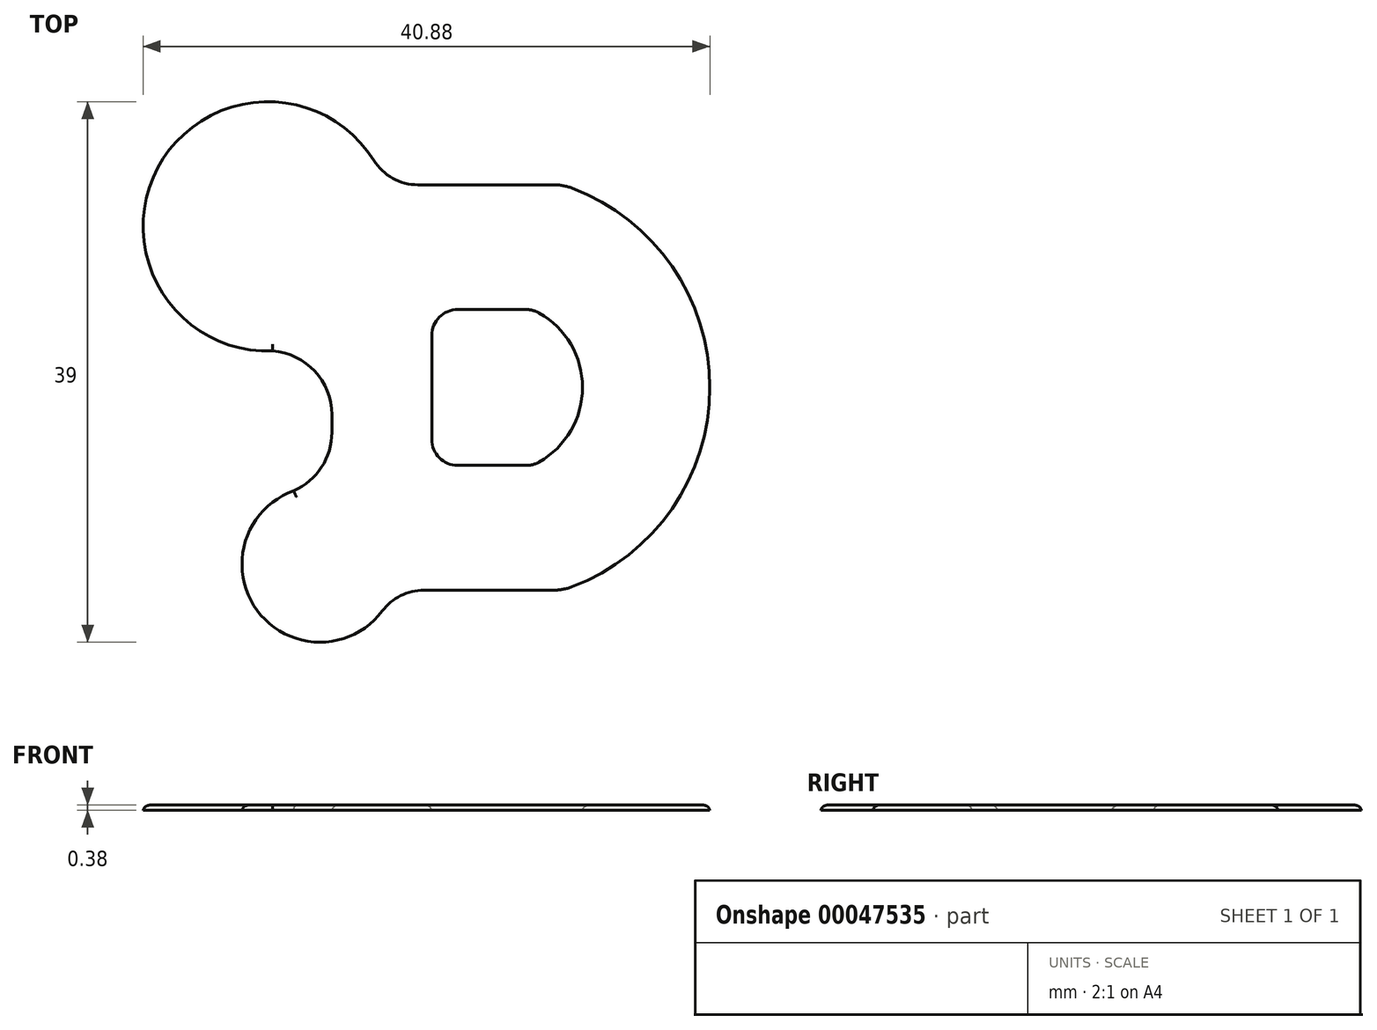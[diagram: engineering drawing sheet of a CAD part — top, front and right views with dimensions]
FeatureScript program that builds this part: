
annotation { "Feature Type Name" : "Feature", "Feature Type Description" : "" }
export const myFeature = defineFeature(function(context is Context, id is Id, definition is map)
    precondition{}
    {
        {
            var Q0;
            Q0=qCreatedBy(makeId("Top.planeOp"),FACE);
            var sketch = newSketch(context, id + "F0", { "sketchPlane" : qUnion([Q0])});
            skArc(sketch, "E0", {"start": v(20.36, 12.7) * mm, "mid": v(-21.2, 11.25) * mm, "end": v(0.9, -23.98) * mm});
            skArc(sketch, "E1", {"start": v(5.1, -50.82) * mm, "mid": v(-2.12, -73.84) * mm, "end": v(22, -74) * mm});
            skArc(sketch, "E2.trimOffspring", {"start": v(52.15, -45.35) * mm, "mid": v(60.5, -31) * mm, "end": v(52.15, -16.65) * mm});
            skArc(sketch, "E3.trimOffspring", {"start": v(58.49, -69.35) * mm, "mid": v(85, -31) * mm, "end": v(58.49, 7.35) * mm});
            skLineSegment(sketch, "E4", {"start": v(31.5, -21) * mm, "end": v(31.5, -41) * mm});
            skLineSegment(sketch, "E5", {"start": v(49.68, -16) * mm, "end": v(36.5, -16) * mm});
            skLineSegment(sketch, "E6", {"start": v(49.68, -46) * mm, "end": v(36.5, -46) * mm});
            skPoint(sketch, "E7.visualSharp", {"position": v(31.5, -16) * mm});
            skArc(sketch, "E7.filletArc", {"start": v(36.5, -16) * mm, "mid": v(32.96, -17.46) * mm, "end": v(31.5, -21) * mm});
            skPoint(sketch, "E8.visualSharp", {"position": v(31.5, -46) * mm});
            skArc(sketch, "E8.filletArc", {"start": v(31.5, -41) * mm, "mid": v(32.96, -44.54) * mm, "end": v(36.5, -46) * mm});
            skPoint(sketch, "E9.visualSharp", {"position": v(50.87, -16) * mm});
            skArc(sketch, "E9.filletArc", {"start": v(52.15, -16.65) * mm, "mid": v(50.96, -16.17) * mm, "end": v(49.68, -16) * mm});
            skPoint(sketch, "E10.visualSharp", {"position": v(50.87, -46) * mm});
            skArc(sketch, "E10.filletArc", {"start": v(49.68, -46) * mm, "mid": v(50.96, -45.83) * mm, "end": v(52.15, -45.35) * mm});
            skLineSegment(sketch, "E11", {"start": v(54.95, 8) * mm, "end": v(28.84, 8) * mm});
            skLineSegment(sketch, "E12", {"start": v(54.95, -70) * mm, "end": v(30, -70) * mm});
            skPoint(sketch, "E13.visualSharp", {"position": v(24.14, -70) * mm});
            skArc(sketch, "E13.filletArc", {"start": v(30, -70) * mm, "mid": v(25.53, -71.06) * mm, "end": v(22, -74) * mm});
            skPoint(sketch, "E14.visualSharp", {"position": v(22.63, 8) * mm});
            skArc(sketch, "E14.filletArc", {"start": v(20.36, 12.7) * mm, "mid": v(24, 9.26) * mm, "end": v(28.84, 8) * mm});
            skPoint(sketch, "E15.visualSharp", {"position": v(56.65, 8) * mm});
            skArc(sketch, "E15.filletArc", {"start": v(58.49, 7.35) * mm, "mid": v(56.75, 7.84) * mm, "end": v(54.95, 8) * mm});
            skPoint(sketch, "E16.visualSharp", {"position": v(56.65, -70) * mm});
            skArc(sketch, "E16.filletArc", {"start": v(54.95, -70) * mm, "mid": v(56.75, -69.84) * mm, "end": v(58.49, -69.35) * mm});
            skArc(sketch, "E17", {"start": v(12.3, -36.25) * mm, "mid": v(8.37, -27.24) * mm, "end": v(-0.9, -23.98) * mm});
            skPoint(sketch, "E18.visualSharp", {"position": v(7.11, -50.28) * mm});
            skArc(sketch, "E19", {"start": v(4.04, -51.23) * mm, "mid": v(10.02, -46.74) * mm, "end": v(12.3, -39.62) * mm});
            skLineSegment(sketch, "E20", {"start": v(12.3, -36.25) * mm, "end": v(12.3, -39.62) * mm});
            skSolve(sketch);
        }
        {
            var Q0;
            Q0=qSketchRegion(id+"F0",true);
            extrude(context, id + "F1", {"entities" : qUnion([Q0]), "depth" : 1 * mm});
        }
        {
            var Q0;
            Q0=makeQuery(id+"F1.opExtrude","SWEPT_BODY",BODY,{"disambiguationData":[OSD([sQuery(id+"F0.wireOp",EDGE,"E0"),sQuery(id+"F0.wireOp",EDGE,"E1"),sQuery(id+"F0.wireOp",EDGE,"E2.trimOffspring"),sQuery(id+"F0.wireOp",EDGE,"E3.trimOffspring"),sQuery(id+"F0.wireOp",EDGE,"E4"),sQuery(id+"F0.wireOp",EDGE,"E5"),sQuery(id+"F0.wireOp",EDGE,"E6"),sQuery(id+"F0.wireOp",EDGE,"E7.filletArc"),sQuery(id+"F0.wireOp",EDGE,"E8.filletArc"),sQuery(id+"F0.wireOp",EDGE,"E9.filletArc"),sQuery(id+"F0.wireOp",EDGE,"E10.filletArc"),sQuery(id+"F0.wireOp",EDGE,"E11"),sQuery(id+"F0.wireOp",EDGE,"E12"),sQuery(id+"F0.wireOp",EDGE,"E13.filletArc"),sQuery(id+"F0.wireOp",EDGE,"E14.filletArc"),sQuery(id+"F0.wireOp",EDGE,"E15.filletArc"),sQuery(id+"F0.wireOp",EDGE,"E16.filletArc"),sQuery(id+"F0.wireOp",EDGE,"E17"),sQuery(id+"F0.wireOp",EDGE,"E19"),sQuery(id+"F0.wireOp",EDGE,"E20")])]});
            var Q1;
            Q1=qCreatedBy(makeId("Origin.pointOp"),VERTEX);
            transform(context, id + "F2", {"entities" : qUnion([Q0]), "transformType" : TransformType.SCALE_UNIFORMLY, "scale" : .5, "makeCopy" : false, "scalePoint" : qUnion([Q1])});
        }
        {
            var Q0;
            Q0=makeQuery(id+"F1.opExtrude","SWEPT_BODY",BODY,{"disambiguationData":[OSD([sQuery(id+"F0.wireOp",EDGE,"E0"),sQuery(id+"F0.wireOp",EDGE,"E1"),sQuery(id+"F0.wireOp",EDGE,"E2.trimOffspring"),sQuery(id+"F0.wireOp",EDGE,"E3.trimOffspring"),sQuery(id+"F0.wireOp",EDGE,"E4"),sQuery(id+"F0.wireOp",EDGE,"E5"),sQuery(id+"F0.wireOp",EDGE,"E6"),sQuery(id+"F0.wireOp",EDGE,"E7.filletArc"),sQuery(id+"F0.wireOp",EDGE,"E8.filletArc"),sQuery(id+"F0.wireOp",EDGE,"E9.filletArc"),sQuery(id+"F0.wireOp",EDGE,"E10.filletArc"),sQuery(id+"F0.wireOp",EDGE,"E11"),sQuery(id+"F0.wireOp",EDGE,"E12"),sQuery(id+"F0.wireOp",EDGE,"E13.filletArc"),sQuery(id+"F0.wireOp",EDGE,"E14.filletArc"),sQuery(id+"F0.wireOp",EDGE,"E15.filletArc"),sQuery(id+"F0.wireOp",EDGE,"E16.filletArc"),sQuery(id+"F0.wireOp",EDGE,"E17"),sQuery(id+"F0.wireOp",EDGE,"E19"),sQuery(id+"F0.wireOp",EDGE,"E20")])]});
            var Q1;
            Q1=qCreatedBy(makeId("Origin.pointOp"),VERTEX);
            transform(context, id + "F3", {"entities" : qUnion([Q0]), "transformType" : TransformType.SCALE_UNIFORMLY, "scale" : .75, "makeCopy" : false, "scalePoint" : qUnion([Q1])});
        }
        {
            var Q0;
            Q0=makeQuery(id+"F1.opExtrude","CAP_FACE",FACE,{"disambiguationData":[OSD([sQuery(id+"F0.wireOp",EDGE,"E0"),sQuery(id+"F0.wireOp",EDGE,"E1"),sQuery(id+"F0.wireOp",EDGE,"E2.trimOffspring"),sQuery(id+"F0.wireOp",EDGE,"E3.trimOffspring"),sQuery(id+"F0.wireOp",EDGE,"E4"),sQuery(id+"F0.wireOp",EDGE,"E5"),sQuery(id+"F0.wireOp",EDGE,"E6"),sQuery(id+"F0.wireOp",EDGE,"E7.filletArc"),sQuery(id+"F0.wireOp",EDGE,"E8.filletArc"),sQuery(id+"F0.wireOp",EDGE,"E9.filletArc"),sQuery(id+"F0.wireOp",EDGE,"E10.filletArc"),sQuery(id+"F0.wireOp",EDGE,"E11"),sQuery(id+"F0.wireOp",EDGE,"E12"),sQuery(id+"F0.wireOp",EDGE,"E13.filletArc"),sQuery(id+"F0.wireOp",EDGE,"E14.filletArc"),sQuery(id+"F0.wireOp",EDGE,"E15.filletArc"),sQuery(id+"F0.wireOp",EDGE,"E16.filletArc"),sQuery(id+"F0.wireOp",EDGE,"E17"),sQuery(id+"F0.wireOp",EDGE,"E19"),sQuery(id+"F0.wireOp",EDGE,"E20")])],"isStart":false});
            fillet(context, id + "F4", {"entities" : qUnion([Q0]), "radius" : .5 * mm, "tangentPropagation" : true, "allowEdgeOverflow" : false});
        }
    });
